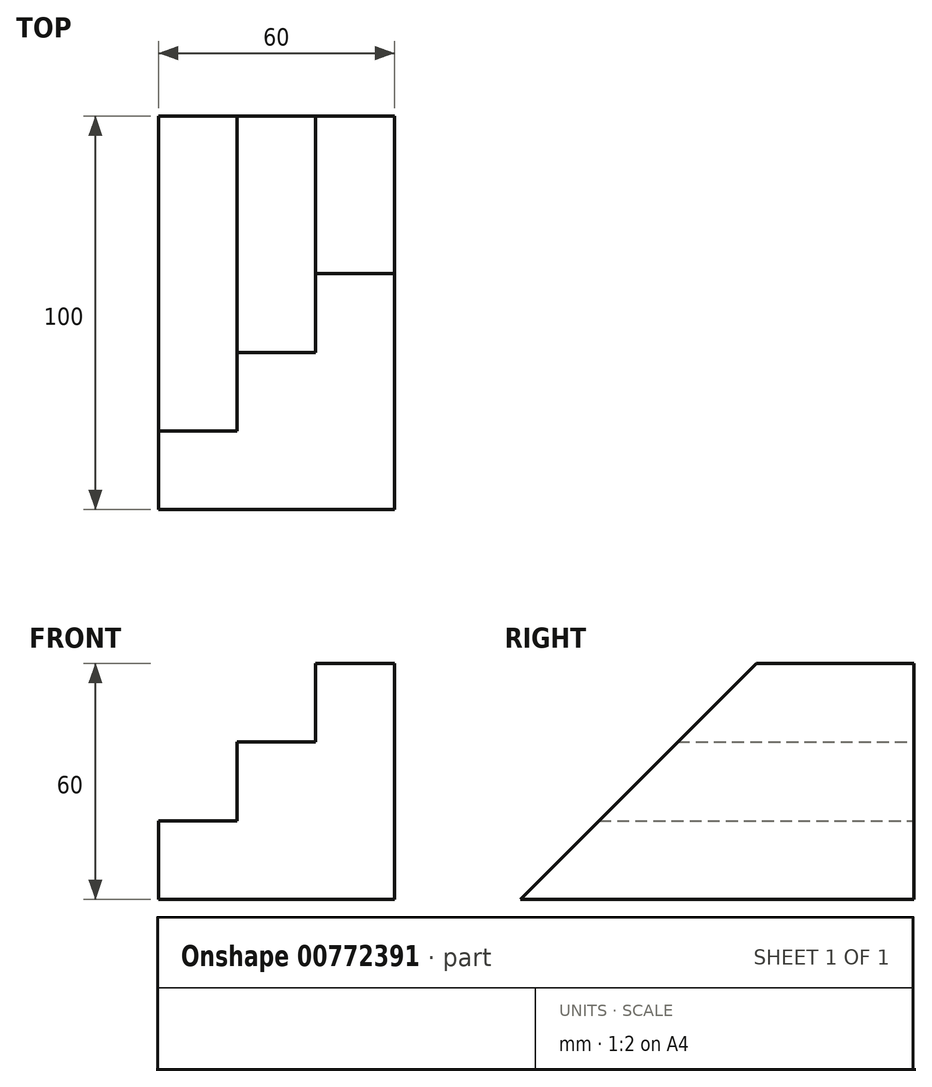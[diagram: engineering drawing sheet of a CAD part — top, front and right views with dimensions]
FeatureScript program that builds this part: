
annotation { "Feature Type Name" : "Feature", "Feature Type Description" : "" }
export const myFeature = defineFeature(function(context is Context, id is Id, definition is map)
    precondition{}
    {
        {
            var Q0;
            Q0=qCreatedBy(makeId("Front.planeOp"),FACE);
            var sketch = newSketch(context, id + "F0", { "sketchPlane" : qUnion([Q0])});
            skLineSegment(sketch, "E0", {"start": v(0, 0) * mm, "end": v(0, 60) * mm});
            skLineSegment(sketch, "E1", {"start": v(0, 60) * mm, "end": v(-20, 60) * mm});
            skLineSegment(sketch, "E2", {"start": v(-20, 60) * mm, "end": v(-20, 40) * mm});
            skLineSegment(sketch, "E3", {"start": v(-20, 40) * mm, "end": v(-40, 40) * mm});
            skLineSegment(sketch, "E4", {"start": v(-40, 40) * mm, "end": v(-40, 20) * mm});
            skLineSegment(sketch, "E5", {"start": v(-40, 20) * mm, "end": v(-60, 20) * mm});
            skLineSegment(sketch, "E6", {"start": v(-60, 20) * mm, "end": v(-60, 0) * mm});
            skLineSegment(sketch, "E7", {"start": v(-60, 0) * mm, "end": v(0, 0) * mm});
            skSolve(sketch);
        }
        {
            var Q0;
            Q0=makeQuery(id+"F0.imprint","IMPRINT",FACE,{"disambiguationData":[TD([[makeQuery(id+"F0.imprint","IMPRINT",EDGE,{"derivedFrom":sQuery(id+"F0.wireOp",EDGE,"E0")}),1.0]])]});
            extrude(context, id + "F1", {"entities" : qUnion([Q0]), "depth" : 100 * mm, "offsetDistance" : 25 * mm});
        }
        {
            var Q0;
            Q0=makeQuery(id+"F1.opExtrude","CAP_EDGE",EDGE,{"disambiguationData":[OSD([sQuery(id+"F0.wireOp",EDGE,"E1")])],"isStart":false});
            chamfer(context, id + "F2", {"entities" : qUnion([Q0]), "width" : 60 * mm, "tangentPropagation" : true});
        }
    });
